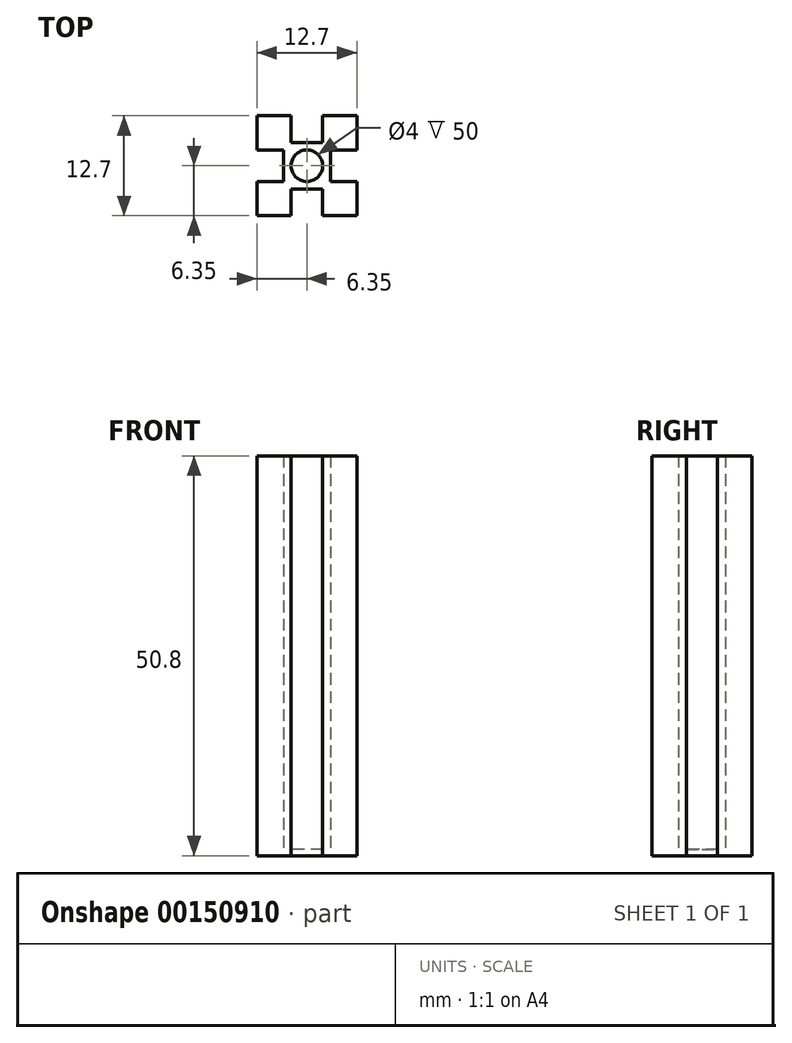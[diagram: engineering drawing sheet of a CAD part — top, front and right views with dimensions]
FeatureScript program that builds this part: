
annotation { "Feature Type Name" : "Feature", "Feature Type Description" : "" }
export const myFeature = defineFeature(function(context is Context, id is Id, definition is map)
    precondition{}
    {
        {
            var Q0;
            Q0=qCreatedBy(makeId("Top.planeOp"),FACE);
            var sketch = newSketch(context, id + "F0", { "sketchPlane" : qUnion([Q0])});
            skLineSegment(sketch, "E0.bottom", {"start": v(-6.35, 6.35) * mm, "end": v(-1.99, 6.35) * mm});
            skLineSegment(sketch, "E0.top", {"start": v(-6.35, -6.35) * mm, "end": v(-1.99, -6.35) * mm});
            skLineSegment(sketch, "E0.left", {"start": v(-6.35, 6.35) * mm, "end": v(-6.35, 1.99) * mm});
            skLineSegment(sketch, "E0.right", {"start": v(6.35, 6.35) * mm, "end": v(6.35, 1.99) * mm});
            skLineSegment(sketch, "E1", {"start": v(-6.35, 6.35) * mm, "end": v(6.35, -6.35) * mm, "construction": true});
            skLineSegment(sketch, "E2.top", {"start": v(-1.99, 2.97) * mm, "end": v(1.99, 2.97) * mm});
            skLineSegment(sketch, "E2.left", {"start": v(-1.99, 6.35) * mm, "end": v(-1.99, 2.97) * mm});
            skLineSegment(sketch, "E2.right", {"start": v(1.99, 6.35) * mm, "end": v(1.99, 2.97) * mm});
            skLineSegment(sketch, "E3.bottom", {"start": v(6.35, 1.99) * mm, "end": v(2.98, 1.99) * mm});
            skLineSegment(sketch, "E3.top", {"start": v(6.35, -1.99) * mm, "end": v(2.98, -1.99) * mm});
            skLineSegment(sketch, "E3.right", {"start": v(2.98, 1.99) * mm, "end": v(2.98, -1.99) * mm});
            skLineSegment(sketch, "E4.top", {"start": v(-1.99, -2.98) * mm, "end": v(1.99, -2.98) * mm});
            skLineSegment(sketch, "E4.left", {"start": v(-1.99, -6.35) * mm, "end": v(-1.99, -2.98) * mm});
            skLineSegment(sketch, "E4.right", {"start": v(1.99, -6.35) * mm, "end": v(1.99, -2.98) * mm});
            skLineSegment(sketch, "E5.bottom", {"start": v(-6.35, -1.99) * mm, "end": v(-2.98, -1.99) * mm});
            skLineSegment(sketch, "E5.top", {"start": v(-6.35, 1.99) * mm, "end": v(-2.98, 1.99) * mm});
            skLineSegment(sketch, "E5.right", {"start": v(-2.98, -1.99) * mm, "end": v(-2.98, 1.99) * mm});
            skLineSegment(sketch, "E6.trimOffspring", {"start": v(-6.35, -1.99) * mm, "end": v(-6.35, -6.35) * mm});
            skLineSegment(sketch, "E7.trimOffspring", {"start": v(1.99, 6.35) * mm, "end": v(6.35, 6.35) * mm});
            skLineSegment(sketch, "E8.trimOffspring", {"start": v(6.35, -1.99) * mm, "end": v(6.35, -6.35) * mm});
            skLineSegment(sketch, "E9.trimOffspring", {"start": v(1.99, -6.35) * mm, "end": v(6.35, -6.35) * mm});
            skSolve(sketch);
        }
        {
            var Q0;
            Q0 = qSketchRegion(id + "F0", true);
            extrude(context, id + "F1", {"entities" : qUnion([Q0]), "depth" : 50.8 * mm});
        }
        {
            var Q0;
            Q0=makeQuery(id+"F1.opExtrude","CAP_FACE",FACE,{"disambiguationData":[OSD([sQuery(id+"F0.wireOp",EDGE,"E0.bottom"),sQuery(id+"F0.wireOp",EDGE,"E0.top"),sQuery(id+"F0.wireOp",EDGE,"E0.left"),sQuery(id+"F0.wireOp",EDGE,"E0.right"),sQuery(id+"F0.wireOp",EDGE,"E2.top"),sQuery(id+"F0.wireOp",EDGE,"E2.left"),sQuery(id+"F0.wireOp",EDGE,"E2.right"),sQuery(id+"F0.wireOp",EDGE,"E3.bottom"),sQuery(id+"F0.wireOp",EDGE,"E3.top"),sQuery(id+"F0.wireOp",EDGE,"E3.right"),sQuery(id+"F0.wireOp",EDGE,"E4.top"),sQuery(id+"F0.wireOp",EDGE,"E4.left"),sQuery(id+"F0.wireOp",EDGE,"E4.right"),sQuery(id+"F0.wireOp",EDGE,"E5.bottom"),sQuery(id+"F0.wireOp",EDGE,"E5.top"),sQuery(id+"F0.wireOp",EDGE,"E5.right"),sQuery(id+"F0.wireOp",EDGE,"E6.trimOffspring"),sQuery(id+"F0.wireOp",EDGE,"E7.trimOffspring"),sQuery(id+"F0.wireOp",EDGE,"E8.trimOffspring"),sQuery(id+"F0.wireOp",EDGE,"E9.trimOffspring")])],"isStart":false});
            var sketch = newSketch(context, id + "F2", { "sketchPlane" : qUnion([Q0])});
            skCircle(sketch, "E10", {"center": v(0, 0) * mm, "radius": 2 * mm});
            skSolve(sketch);
        }
        {
            var Q0;
            Q0 = qSketchRegion(id + "F2", true);
            extrude(context, id + "F3", {"entities" : qUnion([Q0]), "operationType" : NewBodyOperationType.REMOVE, "oppositeDirection" : true, "depth" : 50 * mm});
        }
    });
